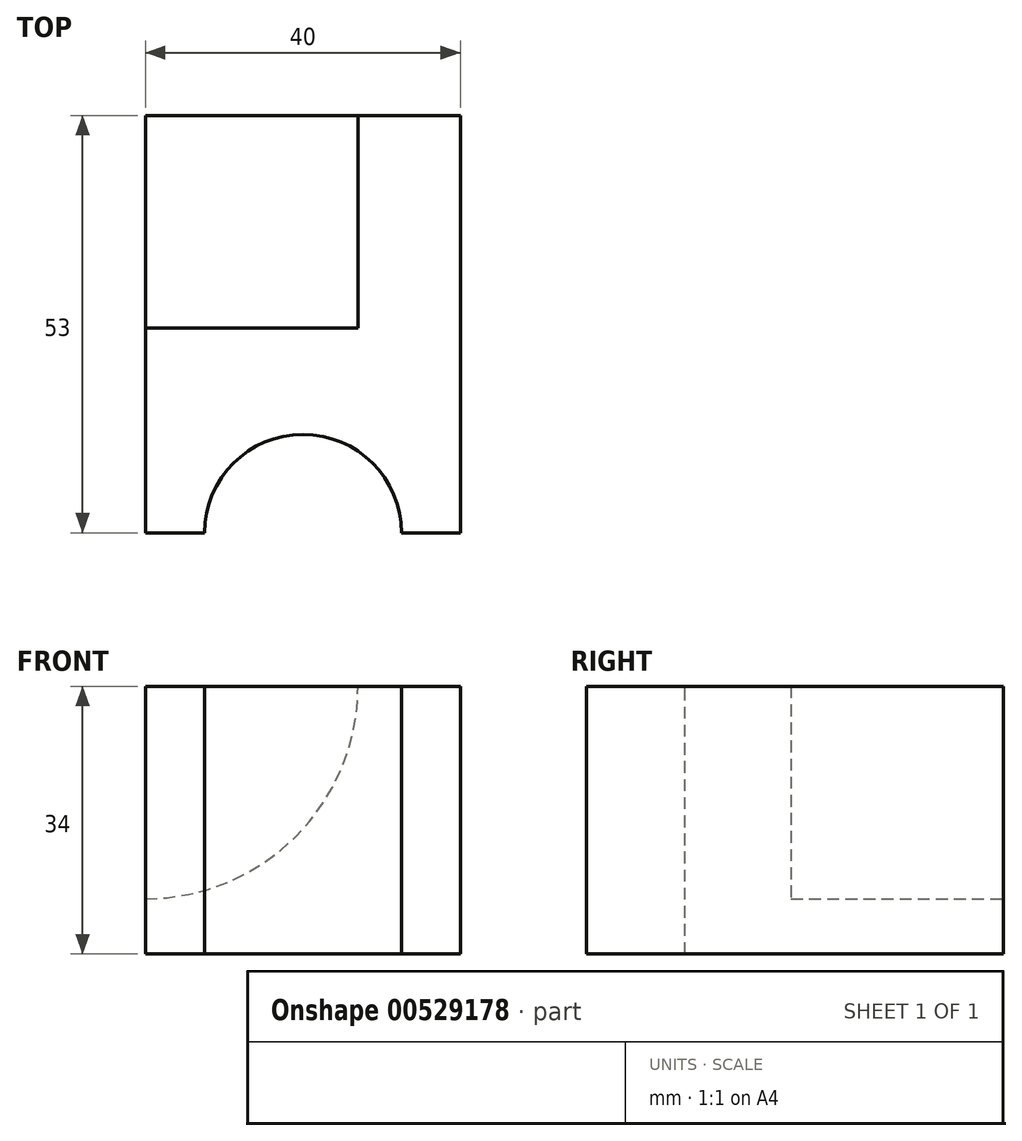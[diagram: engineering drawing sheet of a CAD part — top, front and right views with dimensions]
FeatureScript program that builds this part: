
annotation { "Feature Type Name" : "Feature", "Feature Type Description" : "" }
export const myFeature = defineFeature(function(context is Context, id is Id, definition is map)
    precondition{}
    {
        {
            var Q0;
            Q0=qCreatedBy(makeId("Front.planeOp"),FACE);
            var sketch = newSketch(context, id + "F0", { "sketchPlane" : qUnion([Q0])});
            skLineSegment(sketch, "E0.bottom", {"start": v(20, 17) * mm, "end": v(-20, 17) * mm});
            skLineSegment(sketch, "E0.top", {"start": v(20, -17) * mm, "end": v(-20, -17) * mm});
            skLineSegment(sketch, "E0.left", {"start": v(20, 17) * mm, "end": v(20, -17) * mm});
            skLineSegment(sketch, "E0.right", {"start": v(-20, 17) * mm, "end": v(-20, -17) * mm});
            skPoint(sketch, "E0.middle", {"position": v(0, 0) * mm});
            skSolve(sketch);
        }
        {
            var Q0;
            Q0=makeQuery(id+"F0.imprint","IMPRINT",FACE,{"disambiguationData":[TD([[makeQuery(id+"F0.imprint","IMPRINT",EDGE,{"derivedFrom":sQuery(id+"F0.wireOp",EDGE,"E0.bottom")}),1.0]])]});
            extrude(context, id + "F1", {"entities" : qUnion([Q0]), "endBound" : BoundingType.SYMMETRIC, "depth" : 53 * mm, "offsetDistance" : 25 * mm});
        }
        {
            var Q0;
            Q0=makeQuery(id+"F1.opExtrude","SWEPT_FACE",FACE,{"disambiguationData":[OSD([sQuery(id+"F0.wireOp",EDGE,"E0.bottom")])]});
            var sketch = newSketch(context, id + "F2", { "sketchPlane" : qUnion([Q0])});
            skCircle(sketch, "E1", {"center": v(0, -26.5) * mm, "radius": 12.5 * mm});
            skSolve(sketch);
        }
        {
            var Q0;
            {var subQ0=sQuery(id+"F2.wireOp",EDGE,"E1");var subQ1=makeQuery(id+"F1.opExtrude","CAP_EDGE",EDGE,{"disambiguationData":[OSD([sQuery(id+"F0.wireOp",EDGE,"E0.bottom")])],"isStart":false});var subQ2=makeQuery(id+"F2.imprint","INTERSECT",VERTEX,{"disambiguationData":[OD(0.0)],"derivedFrom":[subQ1,subQ0]});Q0=makeQuery(id+"F2.imprint","IMPRINT",FACE,{"disambiguationData":[TD([[makeQuery(id+"F2.imprint","IMPRINT",EDGE,{"disambiguationData":[TD([[subQ2,-1.0]])],"derivedFrom":subQ0}),1.0]])]});}
            extrude(context, id + "F3", {"entities" : qUnion([Q0]), "operationType" : NewBodyOperationType.REMOVE, "endBound" : BoundingType.THROUGH_ALL, "oppositeDirection" : true, "depth" : 25 * mm, "offsetDistance" : 25 * mm});
        }
        {
            var Q0;
            Q0=makeQuery(id+"F1.opExtrude","CAP_FACE",FACE,{"disambiguationData":[OSD([sQuery(id+"F0.wireOp",EDGE,"E0.bottom"),sQuery(id+"F0.wireOp",EDGE,"E0.top"),sQuery(id+"F0.wireOp",EDGE,"E0.left"),sQuery(id+"F0.wireOp",EDGE,"E0.right")])],"isStart":true});
            var sketch = newSketch(context, id + "F4", { "sketchPlane" : qUnion([Q0])});
            skCircle(sketch, "E2", {"center": v(20, 17) * mm, "radius": 27 * mm});
            skSolve(sketch);
        }
        {
            var Q0;
            {var subQ0=sQuery(id+"F4.wireOp",EDGE,"E2");var subQ1=makeQuery(id+"F1.opExtrude","CAP_EDGE",EDGE,{"disambiguationData":[OSD([sQuery(id+"F0.wireOp",EDGE,"E0.bottom")])],"isStart":true});var subQ2=makeQuery(id+"F4.imprint","INTERSECT",VERTEX,{"derivedFrom":[subQ1,subQ0]});Q0=makeQuery(id+"F4.imprint","IMPRINT",FACE,{"disambiguationData":[TD([[makeQuery(id+"F4.imprint","IMPRINT",EDGE,{"disambiguationData":[TD([[subQ2,-1.0]])],"derivedFrom":subQ0}),1.0]])]});}
            extrude(context, id + "F5", {"entities" : qUnion([Q0]), "operationType" : NewBodyOperationType.REMOVE, "oppositeDirection" : true, "depth" : 27 * mm, "offsetDistance" : 25 * mm});
        }
    });
